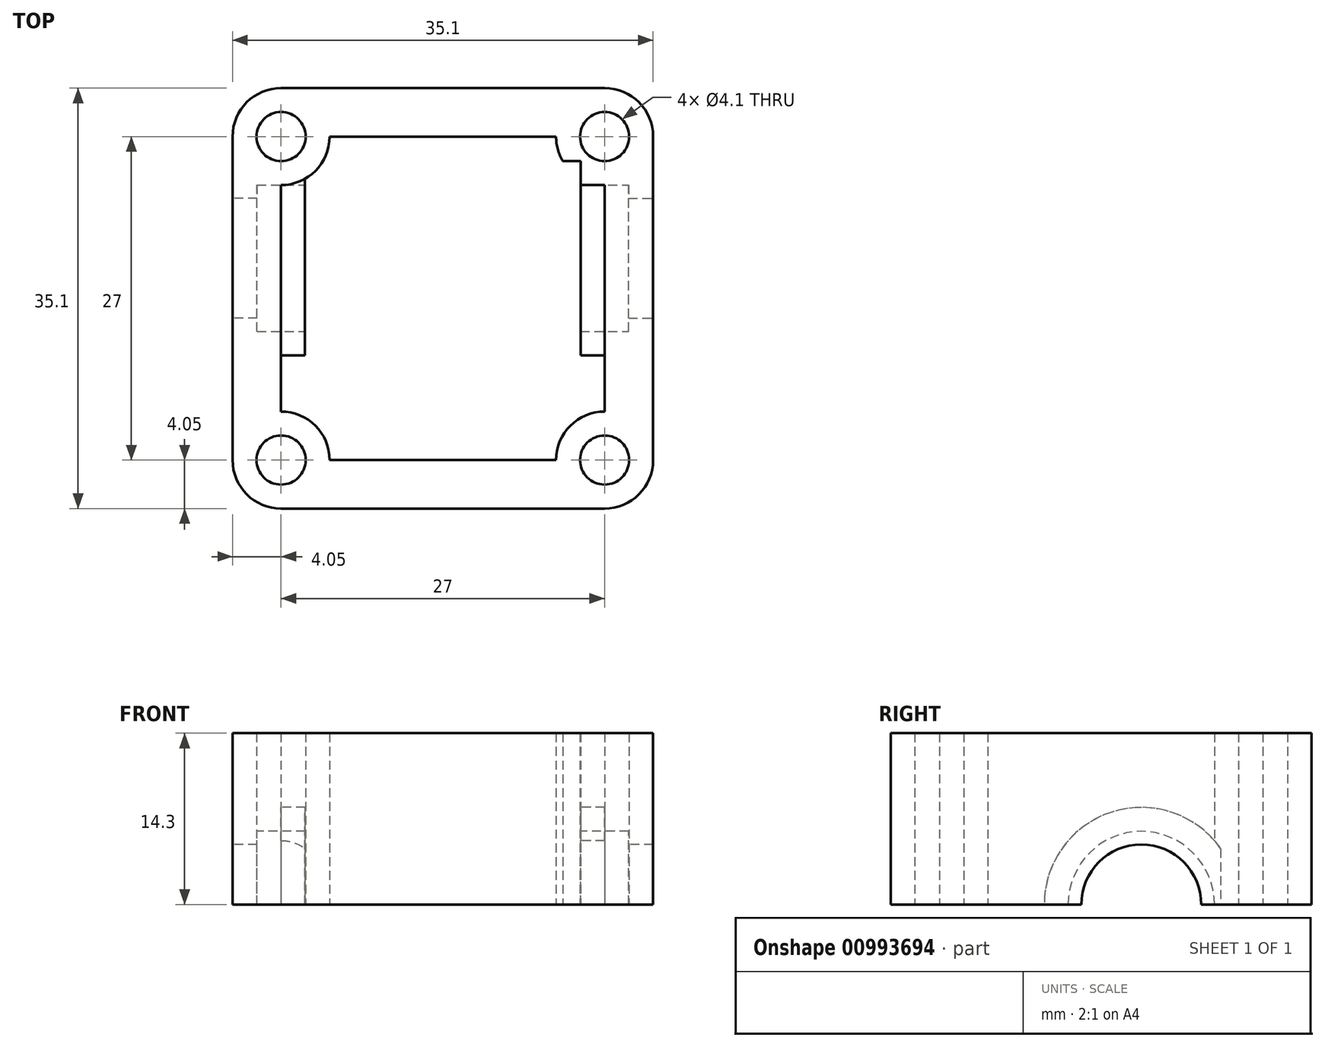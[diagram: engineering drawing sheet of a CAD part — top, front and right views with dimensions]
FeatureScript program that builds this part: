
annotation { "Feature Type Name" : "Feature", "Feature Type Description" : "" }
export const myFeature = defineFeature(function(context is Context, id is Id, definition is map)
    precondition{}
    {
        {
            var Q0;
            Q0=qCreatedBy(makeId("Top.planeOp"),FACE);
            var sketch = newSketch(context, id + "F0", { "sketchPlane" : qUnion([Q0])});
            skLineSegment(sketch, "E0.bottom", {"start": v(17.55, 17.55) * mm, "end": v(-17.55, 17.55) * mm});
            skLineSegment(sketch, "E0.top", {"start": v(17.55, -17.55) * mm, "end": v(-17.55, -17.55) * mm});
            skLineSegment(sketch, "E0.left", {"start": v(17.55, 17.55) * mm, "end": v(17.55, -17.55) * mm});
            skLineSegment(sketch, "E0.right", {"start": v(-17.55, 17.55) * mm, "end": v(-17.55, -17.55) * mm});
            skPoint(sketch, "E0.middle", {"position": v(0, 0) * mm});
            skLineSegment(sketch, "E1", {"start": v(0, 0) * mm, "end": v(0, 17.55) * mm, "construction": true});
            skLineSegment(sketch, "E2", {"start": v(0, 0) * mm, "end": v(-17.55, 0) * mm, "construction": true});
            skLineSegment(sketch, "E3.bottom", {"start": v(13.5, 13.5) * mm, "end": v(-13.5, 13.5) * mm});
            skLineSegment(sketch, "E3.top", {"start": v(13.5, -13.5) * mm, "end": v(-13.5, -13.5) * mm});
            skLineSegment(sketch, "E3.left", {"start": v(13.5, 13.5) * mm, "end": v(13.5, -13.5) * mm});
            skLineSegment(sketch, "E3.right", {"start": v(-13.5, 13.5) * mm, "end": v(-13.5, -13.5) * mm});
            skCircle(sketch, "E4", {"center": v(-13.5, 13.5) * mm, "radius": 2.05 * mm});
            skCircle(sketch, "E5", {"center": v(-13.5, 13.5) * mm, "radius": 4.05 * mm});
            skCircle(sketch, "E6.MirrorC", {"center": v(13.5, 13.5) * mm, "radius": 4.05 * mm});
            skCircle(sketch, "E7.MirrorC", {"center": v(13.5, 13.5) * mm, "radius": 2.05 * mm});
            skCircle(sketch, "E8.MirrorC", {"center": v(-13.5, -13.5) * mm, "radius": 4.05 * mm});
            skCircle(sketch, "E9.MirrorC", {"center": v(-13.5, -13.5) * mm, "radius": 2.05 * mm});
            skCircle(sketch, "E10.MirrorC", {"center": v(13.5, -13.5) * mm, "radius": 4.05 * mm});
            skCircle(sketch, "E11.MirrorC", {"center": v(13.5, -13.5) * mm, "radius": 2.05 * mm});
            skLineSegment(sketch, "E12", {"start": v(-15.5, 11.45) * mm, "end": v(15.5, 11.45) * mm});
            skLineSegment(sketch, "E13", {"start": v(15.5, 11.45) * mm, "end": v(15.5, -4.75) * mm});
            skLineSegment(sketch, "E14", {"start": v(15.5, -4.75) * mm, "end": v(-15.5, -4.75) * mm});
            skLineSegment(sketch, "E15", {"start": v(-15.5, 11.45) * mm, "end": v(-15.5, -4.75) * mm});
            skLineSegment(sketch, "E16", {"start": v(-15.5, 3.35) * mm, "end": v(15.5, 3.35) * mm});
            skLineSegment(sketch, "E17", {"start": v(15.5, -2.75) * mm, "end": v(-15.5, -2.75) * mm});
            skLineSegment(sketch, "E18", {"start": v(-15.5, 9.45) * mm, "end": v(15.5, 9.45) * mm});
            skLineSegment(sketch, "E19", {"start": v(-11.5, 11.45) * mm, "end": v(-11.5, -4.75) * mm});
            skLineSegment(sketch, "E20", {"start": v(11.5, 11.45) * mm, "end": v(11.5, -4.75) * mm});
            skLineSegment(sketch, "E21", {"start": v(-15.5, 3.35) * mm, "end": v(-17.55, 3.35) * mm});
            skLineSegment(sketch, "E22", {"start": v(15.5, 3.35) * mm, "end": v(17.55, 3.35) * mm});
            skLineSegment(sketch, "E23", {"start": v(-15.5, 8.35) * mm, "end": v(-17.55, 8.35) * mm});
            skLineSegment(sketch, "E24", {"start": v(15.5, 8.35) * mm, "end": v(17.55, 8.35) * mm});
            skSolve(sketch);
        }
        {
            var Q0;
            {var subQ0=sQuery(id+"F0.wireOp",EDGE,"E15");var subQ3=sQuery(id+"F0.wireOp",EDGE,"E18");var subQ5=makeQuery(id+"F0.imprint","INTERSECT",VERTEX,{"derivedFrom":[subQ0,subQ3]});Q0=makeQuery(id+"F0.imprint","IMPRINT",FACE,{"disambiguationData":[TD([[makeQuery(id+"F0.imprint","IMPRINT",EDGE,{"disambiguationData":[TD([[subQ5,1.0]])],"derivedFrom":subQ0}),1.0]])]});}
            var Q1;
            {var subQ0=sQuery(id+"F0.wireOp",EDGE,"E5");var subQ3=sQuery(id+"F0.wireOp",EDGE,"E3.bottom");var subQ4=makeQuery(id+"F0.imprint","INTERSECT",VERTEX,{"derivedFrom":[subQ3,subQ0]});Q1=makeQuery(id+"F0.imprint","IMPRINT",FACE,{"disambiguationData":[TD([[makeQuery(id+"F0.imprint","IMPRINT",EDGE,{"disambiguationData":[TD([[subQ4,-1.0]])],"derivedFrom":subQ3}),-1.0]])]});}
            var Q2;
            {var subQ0=sQuery(id+"F0.wireOp",EDGE,"E12");var subQ5=sQuery(id+"F0.wireOp",EDGE,"E15");var subQ7=makeQuery(id+"F0.imprint","INTERSECT",VERTEX,{"derivedFrom":[subQ0,subQ5]});Q2=makeQuery(id+"F0.imprint","IMPRINT",FACE,{"disambiguationData":[TD([[makeQuery(id+"F0.imprint","IMPRINT",EDGE,{"disambiguationData":[TD([[subQ7,-1.0]])],"derivedFrom":subQ5}),1.0]])]});}
            var Q3;
            {var subQ1=sQuery(id+"F0.wireOp",EDGE,"E0.right");var subQ7=sQuery(id+"F0.wireOp",EDGE,"E5");var subQ8=makeQuery(id+"F0.imprint","INTERSECT",VERTEX,{"derivedFrom":[subQ1,subQ7]});Q3=makeQuery(id+"F0.imprint","IMPRINT",FACE,{"disambiguationData":[TD([[makeQuery(id+"F0.imprint","IMPRINT",EDGE,{"disambiguationData":[TD([[subQ8,-1.0]])],"derivedFrom":subQ1}),1.0]])]});}
            var Q4;
            {var subQ0=sQuery(id+"F0.wireOp",EDGE,"E17");var subQ5=sQuery(id+"F0.wireOp",EDGE,"E15");var subQ7=makeQuery(id+"F0.imprint","INTERSECT",VERTEX,{"derivedFrom":[subQ5,subQ0]});Q4=makeQuery(id+"F0.imprint","IMPRINT",FACE,{"disambiguationData":[TD([[makeQuery(id+"F0.imprint","IMPRINT",EDGE,{"disambiguationData":[TD([[subQ7,1.0]])],"derivedFrom":subQ5}),1.0]])]});}
            var Q5;
            {var subQ0=sQuery(id+"F0.wireOp",EDGE,"E17");var subQ1=sQuery(id+"F0.wireOp",EDGE,"E3.right");var subQ2=makeQuery(id+"F0.imprint","INTERSECT",VERTEX,{"derivedFrom":[subQ1,subQ0]});Q5=makeQuery(id+"F0.imprint","IMPRINT",FACE,{"disambiguationData":[TD([[makeQuery(id+"F0.imprint","IMPRINT",EDGE,{"disambiguationData":[TD([[subQ2,-1.0]])],"derivedFrom":subQ1}),-1.0]])]});}
            var Q6;
            {var subQ0=sQuery(id+"F0.wireOp",EDGE,"E8.MirrorC");var subQ2=sQuery(id+"F0.wireOp",EDGE,"E3.top");var subQ3=makeQuery(id+"F0.imprint","INTERSECT",VERTEX,{"derivedFrom":[subQ2,subQ0]});Q6=makeQuery(id+"F0.imprint","IMPRINT",FACE,{"disambiguationData":[TD([[makeQuery(id+"F0.imprint","IMPRINT",EDGE,{"disambiguationData":[TD([[subQ3,-1.0]])],"derivedFrom":subQ2}),1.0]])]});}
            var Q7;
            {var subQ0=sQuery(id+"F0.wireOp",EDGE,"E10.MirrorC");var subQ1=sQuery(id+"F0.wireOp",EDGE,"E0.top");var subQ2=makeQuery(id+"F0.imprint","INTERSECT",VERTEX,{"derivedFrom":[subQ1,subQ0]});Q7=makeQuery(id+"F0.imprint","IMPRINT",FACE,{"disambiguationData":[TD([[makeQuery(id+"F0.imprint","IMPRINT",EDGE,{"disambiguationData":[TD([[subQ2,-1.0]])],"derivedFrom":subQ1}),-1.0]])]});}
            var Q8;
            {var subQ0=sQuery(id+"F0.wireOp",EDGE,"E8.MirrorC");var subQ1=sQuery(id+"F0.wireOp",EDGE,"E3.top");var subQ2=makeQuery(id+"F0.imprint","INTERSECT",VERTEX,{"derivedFrom":[subQ1,subQ0]});Q8=makeQuery(id+"F0.imprint","IMPRINT",FACE,{"disambiguationData":[TD([[makeQuery(id+"F0.imprint","IMPRINT",EDGE,{"disambiguationData":[TD([[subQ2,-1.0]])],"derivedFrom":subQ1}),-1.0]])]});}
            var Q9;
            {var subQ3=sQuery(id+"F0.wireOp",EDGE,"E3.top");var subQ7=sQuery(id+"F0.wireOp",EDGE,"E11.MirrorC");var subQ9=makeQuery(id+"F0.imprint","INTERSECT",VERTEX,{"derivedFrom":[subQ3,subQ7]});Q9=makeQuery(id+"F0.imprint","IMPRINT",FACE,{"disambiguationData":[TD([[makeQuery(id+"F0.imprint","IMPRINT",EDGE,{"disambiguationData":[TD([[subQ9,-1.0]])],"derivedFrom":subQ3}),1.0]])]});}
            var Q10;
            {var subQ0=sQuery(id+"F0.wireOp",EDGE,"E11.MirrorC");var subQ1=sQuery(id+"F0.wireOp",EDGE,"E3.top");var subQ2=makeQuery(id+"F0.imprint","INTERSECT",VERTEX,{"derivedFrom":[subQ1,subQ0]});Q10=makeQuery(id+"F0.imprint","IMPRINT",FACE,{"disambiguationData":[TD([[makeQuery(id+"F0.imprint","IMPRINT",EDGE,{"disambiguationData":[TD([[subQ2,-1.0]])],"derivedFrom":subQ1}),-1.0]])]});}
            var Q11;
            {var subQ5=sQuery(id+"F0.wireOp",EDGE,"E0.left");var subQ7=sQuery(id+"F0.wireOp",EDGE,"E6.MirrorC");var subQ8=makeQuery(id+"F0.imprint","INTERSECT",VERTEX,{"derivedFrom":[subQ5,subQ7]});Q11=makeQuery(id+"F0.imprint","IMPRINT",FACE,{"disambiguationData":[TD([[makeQuery(id+"F0.imprint","IMPRINT",EDGE,{"disambiguationData":[TD([[subQ8,-1.0]])],"derivedFrom":subQ5}),-1.0]])]});}
            var Q12;
            {var subQ0=sQuery(id+"F0.wireOp",EDGE,"E17");var subQ1=sQuery(id+"F0.wireOp",EDGE,"E3.left");var subQ2=makeQuery(id+"F0.imprint","INTERSECT",VERTEX,{"derivedFrom":[subQ1,subQ0]});Q12=makeQuery(id+"F0.imprint","IMPRINT",FACE,{"disambiguationData":[TD([[makeQuery(id+"F0.imprint","IMPRINT",EDGE,{"disambiguationData":[TD([[subQ2,-1.0]])],"derivedFrom":subQ1}),1.0]])]});}
            var Q13;
            {var subQ0=sQuery(id+"F0.wireOp",EDGE,"E17");var subQ5=sQuery(id+"F0.wireOp",EDGE,"E13");var subQ6=makeQuery(id+"F0.imprint","INTERSECT",VERTEX,{"derivedFrom":[subQ5,subQ0]});Q13=makeQuery(id+"F0.imprint","IMPRINT",FACE,{"disambiguationData":[TD([[makeQuery(id+"F0.imprint","IMPRINT",EDGE,{"disambiguationData":[TD([[subQ6,1.0]])],"derivedFrom":subQ5}),-1.0]])]});}
            var Q14;
            {var subQ0=sQuery(id+"F0.wireOp",EDGE,"E13");var subQ3=sQuery(id+"F0.wireOp",EDGE,"E18");var subQ5=makeQuery(id+"F0.imprint","INTERSECT",VERTEX,{"derivedFrom":[subQ0,subQ3]});Q14=makeQuery(id+"F0.imprint","IMPRINT",FACE,{"disambiguationData":[TD([[makeQuery(id+"F0.imprint","IMPRINT",EDGE,{"disambiguationData":[TD([[subQ5,1.0]])],"derivedFrom":subQ0}),-1.0]])]});}
            var Q15;
            {var subQ0=sQuery(id+"F0.wireOp",EDGE,"E12");var subQ5=sQuery(id+"F0.wireOp",EDGE,"E13");var subQ7=makeQuery(id+"F0.imprint","INTERSECT",VERTEX,{"derivedFrom":[subQ0,subQ5]});Q15=makeQuery(id+"F0.imprint","IMPRINT",FACE,{"disambiguationData":[TD([[makeQuery(id+"F0.imprint","IMPRINT",EDGE,{"disambiguationData":[TD([[subQ7,-1.0]])],"derivedFrom":subQ5}),-1.0]])]});}
            var Q16;
            {var subQ0=sQuery(id+"F0.wireOp",EDGE,"E12");var subQ5=sQuery(id+"F0.wireOp",EDGE,"E20");var subQ7=makeQuery(id+"F0.imprint","INTERSECT",VERTEX,{"derivedFrom":[subQ0,subQ5]});Q16=makeQuery(id+"F0.imprint","IMPRINT",FACE,{"disambiguationData":[TD([[makeQuery(id+"F0.imprint","IMPRINT",EDGE,{"disambiguationData":[TD([[subQ7,-1.0]])],"derivedFrom":subQ5}),1.0]])]});}
            var Q17;
            {var subQ0=sQuery(id+"F0.wireOp",EDGE,"E20");var subQ1=sQuery(id+"F0.wireOp",EDGE,"E6.MirrorC");var subQ2=makeQuery(id+"F0.imprint","INTERSECT",VERTEX,{"derivedFrom":[subQ1,subQ0]});Q17=makeQuery(id+"F0.imprint","IMPRINT",FACE,{"disambiguationData":[TD([[makeQuery(id+"F0.imprint","IMPRINT",EDGE,{"disambiguationData":[TD([[subQ2,-1.0]])],"derivedFrom":subQ1}),-1.0]])]});}
            var Q18;
            {var subQ4=sQuery(id+"F0.wireOp",EDGE,"E3.bottom");var subQ6=sQuery(id+"F0.wireOp",EDGE,"E7.MirrorC");var subQ7=makeQuery(id+"F0.imprint","INTERSECT",VERTEX,{"derivedFrom":[subQ4,subQ6]});Q18=makeQuery(id+"F0.imprint","IMPRINT",FACE,{"disambiguationData":[TD([[makeQuery(id+"F0.imprint","IMPRINT",EDGE,{"disambiguationData":[TD([[subQ7,-1.0]])],"derivedFrom":subQ4}),1.0]])]});}
            var Q19;
            {var subQ5=sQuery(id+"F0.wireOp",EDGE,"E7.MirrorC");var subQ6=sQuery(id+"F0.wireOp",EDGE,"E3.bottom");var subQ7=makeQuery(id+"F0.imprint","INTERSECT",VERTEX,{"derivedFrom":[subQ6,subQ5]});Q19=makeQuery(id+"F0.imprint","IMPRINT",FACE,{"disambiguationData":[TD([[makeQuery(id+"F0.imprint","IMPRINT",EDGE,{"disambiguationData":[TD([[subQ7,-1.0]])],"derivedFrom":subQ6}),-1.0]])]});}
            var Q20;
            {var subQ0=sQuery(id+"F0.wireOp",EDGE,"E6.MirrorC");var subQ1=sQuery(id+"F0.wireOp",EDGE,"E0.bottom");var subQ2=makeQuery(id+"F0.imprint","INTERSECT",VERTEX,{"derivedFrom":[subQ1,subQ0]});Q20=makeQuery(id+"F0.imprint","IMPRINT",FACE,{"disambiguationData":[TD([[makeQuery(id+"F0.imprint","IMPRINT",EDGE,{"disambiguationData":[TD([[subQ2,-1.0]])],"derivedFrom":subQ1}),1.0]])]});}
            var Q21;
            {var subQ0=sQuery(id+"F0.wireOp",EDGE,"E5");var subQ1=sQuery(id+"F0.wireOp",EDGE,"E3.bottom");var subQ2=makeQuery(id+"F0.imprint","INTERSECT",VERTEX,{"derivedFrom":[subQ1,subQ0]});Q21=makeQuery(id+"F0.imprint","IMPRINT",FACE,{"disambiguationData":[TD([[makeQuery(id+"F0.imprint","IMPRINT",EDGE,{"disambiguationData":[TD([[subQ2,-1.0]])],"derivedFrom":subQ1}),1.0]])]});}
            var Q22;
            {var subQ0=sQuery(id+"F0.wireOp",EDGE,"E12");var subQ5=sQuery(id+"F0.wireOp",EDGE,"E19");var subQ7=makeQuery(id+"F0.imprint","INTERSECT",VERTEX,{"derivedFrom":[subQ0,subQ5]});Q22=makeQuery(id+"F0.imprint","IMPRINT",FACE,{"disambiguationData":[TD([[makeQuery(id+"F0.imprint","IMPRINT",EDGE,{"disambiguationData":[TD([[subQ7,-1.0]])],"derivedFrom":subQ5}),-1.0]])]});}
            var Q23;
            {var subQ0=sQuery(id+"F0.wireOp",EDGE,"E19");var subQ1=sQuery(id+"F0.wireOp",EDGE,"E5");var subQ2=makeQuery(id+"F0.imprint","INTERSECT",VERTEX,{"derivedFrom":[subQ1,subQ0]});Q23=makeQuery(id+"F0.imprint","IMPRINT",FACE,{"disambiguationData":[TD([[makeQuery(id+"F0.imprint","IMPRINT",EDGE,{"disambiguationData":[TD([[subQ2,-1.0]])],"derivedFrom":subQ1}),1.0]])]});}
            var Q24;
            {var subQ10=sQuery(id+"F0.wireOp",EDGE,"E21");Q24=makeQuery(id+"F0.imprint","IMPRINT",FACE,{"disambiguationData":[TD([[makeQuery(id+"F0.imprint","IMPRINT",EDGE,{"derivedFrom":subQ10}),1.0]])]});}
            var Q25;
            {var subQ0=sQuery(id+"F0.wireOp",EDGE,"E21");Q25=makeQuery(id+"F0.imprint","IMPRINT",FACE,{"disambiguationData":[TD([[makeQuery(id+"F0.imprint","IMPRINT",EDGE,{"derivedFrom":subQ0}),-1.0]])]});}
            var Q26;
            {var subQ1=sQuery(id+"F0.wireOp",EDGE,"E15");var subQ4=sQuery(id+"F0.wireOp",EDGE,"E18");var subQ5=makeQuery(id+"F0.imprint","INTERSECT",VERTEX,{"derivedFrom":[subQ1,subQ4]});Q26=makeQuery(id+"F0.imprint","IMPRINT",FACE,{"disambiguationData":[TD([[makeQuery(id+"F0.imprint","IMPRINT",EDGE,{"disambiguationData":[TD([[subQ5,-1.0]])],"derivedFrom":subQ1}),1.0]])]});}
            var Q27;
            {var subQ0=sQuery(id+"F0.wireOp",EDGE,"E22");Q27=makeQuery(id+"F0.imprint","IMPRINT",FACE,{"disambiguationData":[TD([[makeQuery(id+"F0.imprint","IMPRINT",EDGE,{"derivedFrom":subQ0}),1.0]])]});}
            var Q28;
            {var subQ1=sQuery(id+"F0.wireOp",EDGE,"E13");var subQ6=sQuery(id+"F0.wireOp",EDGE,"E18");var subQ7=makeQuery(id+"F0.imprint","INTERSECT",VERTEX,{"derivedFrom":[subQ1,subQ6]});Q28=makeQuery(id+"F0.imprint","IMPRINT",FACE,{"disambiguationData":[TD([[makeQuery(id+"F0.imprint","IMPRINT",EDGE,{"disambiguationData":[TD([[subQ7,-1.0]])],"derivedFrom":subQ1}),-1.0]])]});}
            var Q29;
            {var subQ0=sQuery(id+"F0.wireOp",EDGE,"E22");Q29=makeQuery(id+"F0.imprint","IMPRINT",FACE,{"disambiguationData":[TD([[makeQuery(id+"F0.imprint","IMPRINT",EDGE,{"derivedFrom":subQ0}),-1.0]])]});}
            var Q30;
            {var subQ0=sQuery(id+"F0.wireOp",EDGE,"E18");var subQ1=sQuery(id+"F0.wireOp",EDGE,"E5");var subQ2=makeQuery(id+"F0.imprint","INTERSECT",VERTEX,{"derivedFrom":[subQ1,subQ0]});Q30=makeQuery(id+"F0.imprint","IMPRINT",FACE,{"disambiguationData":[TD([[makeQuery(id+"F0.imprint","IMPRINT",EDGE,{"disambiguationData":[TD([[subQ2,-1.0]])],"derivedFrom":subQ1}),1.0]])]});}
            var Q31;
            {var subQ4=sQuery(id+"F0.wireOp",EDGE,"E5");var subQ6=sQuery(id+"F0.wireOp",EDGE,"E3.right");var subQ7=makeQuery(id+"F0.imprint","INTERSECT",VERTEX,{"derivedFrom":[subQ6,subQ4]});Q31=makeQuery(id+"F0.imprint","IMPRINT",FACE,{"disambiguationData":[TD([[makeQuery(id+"F0.imprint","IMPRINT",EDGE,{"disambiguationData":[TD([[subQ7,-1.0]])],"derivedFrom":subQ6}),-1.0]])]});}
            var Q32;
            {var subQ4=sQuery(id+"F0.wireOp",EDGE,"E6.MirrorC");var subQ6=sQuery(id+"F0.wireOp",EDGE,"E3.left");var subQ7=makeQuery(id+"F0.imprint","INTERSECT",VERTEX,{"derivedFrom":[subQ6,subQ4]});Q32=makeQuery(id+"F0.imprint","IMPRINT",FACE,{"disambiguationData":[TD([[makeQuery(id+"F0.imprint","IMPRINT",EDGE,{"disambiguationData":[TD([[subQ7,-1.0]])],"derivedFrom":subQ6}),1.0]])]});}
            var Q33;
            {var subQ0=sQuery(id+"F0.wireOp",EDGE,"E18");var subQ1=sQuery(id+"F0.wireOp",EDGE,"E6.MirrorC");var subQ2=makeQuery(id+"F0.imprint","INTERSECT",VERTEX,{"derivedFrom":[subQ1,subQ0]});Q33=makeQuery(id+"F0.imprint","IMPRINT",FACE,{"disambiguationData":[TD([[makeQuery(id+"F0.imprint","IMPRINT",EDGE,{"disambiguationData":[TD([[subQ2,-1.0]])],"derivedFrom":subQ1}),-1.0]])]});}
            extrude(context, id + "F1", {"entities" : qUnion([Q0, Q1, Q2, Q3, Q4, Q5, Q6, Q7, Q8, Q9, Q10, Q11, Q12, Q13, Q14, Q15, Q16, Q17, Q18, Q19, Q20, Q21, Q22, Q23, Q24, Q25, Q26, Q27, Q28, Q29, Q30, Q31, Q32, Q33]), "depth" : ((28 / 2) + 0.3) * mm, "offsetDistance" : 25 * mm});
        }
        {
            var Q0;
            {var subQ0=sQuery(id+"F0.wireOp",EDGE,"E21");Q0=makeQuery(id+"F0.imprint","IMPRINT",FACE,{"disambiguationData":[TD([[makeQuery(id+"F0.imprint","IMPRINT",EDGE,{"derivedFrom":subQ0}),-1.0]])]});}
            var Q1;
            {var subQ1=sQuery(id+"F0.wireOp",EDGE,"E15");var subQ4=sQuery(id+"F0.wireOp",EDGE,"E18");var subQ5=makeQuery(id+"F0.imprint","INTERSECT",VERTEX,{"derivedFrom":[subQ1,subQ4]});Q1=makeQuery(id+"F0.imprint","IMPRINT",FACE,{"disambiguationData":[TD([[makeQuery(id+"F0.imprint","IMPRINT",EDGE,{"disambiguationData":[TD([[subQ5,-1.0]])],"derivedFrom":subQ1}),1.0]])]});}
            var Q2;
            {var subQ0=sQuery(id+"F0.wireOp",EDGE,"E16");var subQ1=sQuery(id+"F0.wireOp",EDGE,"E3.right");var subQ2=makeQuery(id+"F0.imprint","INTERSECT",VERTEX,{"derivedFrom":[subQ1,subQ0]});Q2=makeQuery(id+"F0.imprint","IMPRINT",FACE,{"disambiguationData":[TD([[makeQuery(id+"F0.imprint","IMPRINT",EDGE,{"disambiguationData":[TD([[subQ2,-1.0]])],"derivedFrom":subQ0}),1.0]])]});}
            var Q3;
            {var subQ0=sQuery(id+"F0.wireOp",EDGE,"E12");var subQ5=sQuery(id+"F0.wireOp",EDGE,"E19");var subQ7=makeQuery(id+"F0.imprint","INTERSECT",VERTEX,{"derivedFrom":[subQ0,subQ5]});Q3=makeQuery(id+"F0.imprint","IMPRINT",FACE,{"disambiguationData":[TD([[makeQuery(id+"F0.imprint","IMPRINT",EDGE,{"disambiguationData":[TD([[subQ7,-1.0]])],"derivedFrom":subQ5}),-1.0]])]});}
            var Q4;
            {var subQ0=sQuery(id+"F0.wireOp",EDGE,"E12");var subQ5=sQuery(id+"F0.wireOp",EDGE,"E15");var subQ6=makeQuery(id+"F0.imprint","INTERSECT",VERTEX,{"derivedFrom":[subQ0,subQ5]});Q4=makeQuery(id+"F0.imprint","IMPRINT",FACE,{"disambiguationData":[TD([[makeQuery(id+"F0.imprint","IMPRINT",EDGE,{"disambiguationData":[TD([[subQ6,-1.0]])],"derivedFrom":subQ5}),1.0]])]});}
            var Q5;
            {var subQ0=sQuery(id+"F0.wireOp",EDGE,"E12");var subQ5=sQuery(id+"F0.wireOp",EDGE,"E20");var subQ6=makeQuery(id+"F0.imprint","INTERSECT",VERTEX,{"derivedFrom":[subQ0,subQ5]});Q5=makeQuery(id+"F0.imprint","IMPRINT",FACE,{"disambiguationData":[TD([[makeQuery(id+"F0.imprint","IMPRINT",EDGE,{"disambiguationData":[TD([[subQ6,-1.0]])],"derivedFrom":subQ5}),1.0]])]});}
            var Q6;
            {var subQ0=sQuery(id+"F0.wireOp",EDGE,"E16");var subQ1=sQuery(id+"F0.wireOp",EDGE,"E3.left");var subQ2=makeQuery(id+"F0.imprint","INTERSECT",VERTEX,{"derivedFrom":[subQ1,subQ0]});Q6=makeQuery(id+"F0.imprint","IMPRINT",FACE,{"disambiguationData":[TD([[makeQuery(id+"F0.imprint","IMPRINT",EDGE,{"disambiguationData":[TD([[subQ2,1.0]])],"derivedFrom":subQ0}),1.0]])]});}
            var Q7;
            {var subQ1=sQuery(id+"F0.wireOp",EDGE,"E13");var subQ6=sQuery(id+"F0.wireOp",EDGE,"E18");var subQ7=makeQuery(id+"F0.imprint","INTERSECT",VERTEX,{"derivedFrom":[subQ1,subQ6]});Q7=makeQuery(id+"F0.imprint","IMPRINT",FACE,{"disambiguationData":[TD([[makeQuery(id+"F0.imprint","IMPRINT",EDGE,{"disambiguationData":[TD([[subQ7,-1.0]])],"derivedFrom":subQ1}),-1.0]])]});}
            var Q8;
            {var subQ0=sQuery(id+"F0.wireOp",EDGE,"E12");var subQ5=sQuery(id+"F0.wireOp",EDGE,"E13");var subQ7=makeQuery(id+"F0.imprint","INTERSECT",VERTEX,{"derivedFrom":[subQ0,subQ5]});Q8=makeQuery(id+"F0.imprint","IMPRINT",FACE,{"disambiguationData":[TD([[makeQuery(id+"F0.imprint","IMPRINT",EDGE,{"disambiguationData":[TD([[subQ7,-1.0]])],"derivedFrom":subQ5}),-1.0]])]});}
            var Q9;
            {var subQ0=sQuery(id+"F0.wireOp",EDGE,"E22");Q9=makeQuery(id+"F0.imprint","IMPRINT",FACE,{"disambiguationData":[TD([[makeQuery(id+"F0.imprint","IMPRINT",EDGE,{"derivedFrom":subQ0}),1.0]])]});}
            var Q10;
            {var subQ0=sQuery(id+"F0.wireOp",EDGE,"E19");var subQ1=sQuery(id+"F0.wireOp",EDGE,"E5");var subQ2=makeQuery(id+"F0.imprint","INTERSECT",VERTEX,{"derivedFrom":[subQ1,subQ0]});Q10=makeQuery(id+"F0.imprint","IMPRINT",FACE,{"disambiguationData":[TD([[makeQuery(id+"F0.imprint","IMPRINT",EDGE,{"disambiguationData":[TD([[subQ2,-1.0]])],"derivedFrom":subQ0}),-1.0]])]});}
            var Q11;
            {var subQ0=sQuery(id+"F0.wireOp",EDGE,"E15");var subQ3=sQuery(id+"F0.wireOp",EDGE,"E18");var subQ5=makeQuery(id+"F0.imprint","INTERSECT",VERTEX,{"derivedFrom":[subQ0,subQ3]});Q11=makeQuery(id+"F0.imprint","IMPRINT",FACE,{"disambiguationData":[TD([[makeQuery(id+"F0.imprint","IMPRINT",EDGE,{"disambiguationData":[TD([[subQ5,1.0]])],"derivedFrom":subQ0}),1.0]])]});}
            var Q12;
            {var subQ0=sQuery(id+"F0.wireOp",EDGE,"E13");var subQ3=sQuery(id+"F0.wireOp",EDGE,"E18");var subQ5=makeQuery(id+"F0.imprint","INTERSECT",VERTEX,{"derivedFrom":[subQ0,subQ3]});Q12=makeQuery(id+"F0.imprint","IMPRINT",FACE,{"disambiguationData":[TD([[makeQuery(id+"F0.imprint","IMPRINT",EDGE,{"disambiguationData":[TD([[subQ5,1.0]])],"derivedFrom":subQ0}),-1.0]])]});}
            var Q13;
            {var subQ0=sQuery(id+"F0.wireOp",EDGE,"E20");var subQ1=sQuery(id+"F0.wireOp",EDGE,"E6.MirrorC");var subQ2=makeQuery(id+"F0.imprint","INTERSECT",VERTEX,{"derivedFrom":[subQ1,subQ0]});Q13=makeQuery(id+"F0.imprint","IMPRINT",FACE,{"disambiguationData":[TD([[makeQuery(id+"F0.imprint","IMPRINT",EDGE,{"disambiguationData":[TD([[subQ2,-1.0]])],"derivedFrom":subQ0}),1.0]])]});}
            var Q14;
            {var subQ4=sQuery(id+"F0.wireOp",EDGE,"E5");var subQ6=sQuery(id+"F0.wireOp",EDGE,"E3.right");var subQ7=makeQuery(id+"F0.imprint","INTERSECT",VERTEX,{"derivedFrom":[subQ6,subQ4]});Q14=makeQuery(id+"F0.imprint","IMPRINT",FACE,{"disambiguationData":[TD([[makeQuery(id+"F0.imprint","IMPRINT",EDGE,{"disambiguationData":[TD([[subQ7,-1.0]])],"derivedFrom":subQ6}),-1.0]])]});}
            var Q15;
            {var subQ0=sQuery(id+"F0.wireOp",EDGE,"E18");var subQ1=sQuery(id+"F0.wireOp",EDGE,"E3.right");var subQ2=makeQuery(id+"F0.imprint","INTERSECT",VERTEX,{"derivedFrom":[subQ1,subQ0]});Q15=makeQuery(id+"F0.imprint","IMPRINT",FACE,{"disambiguationData":[TD([[makeQuery(id+"F0.imprint","IMPRINT",EDGE,{"disambiguationData":[TD([[subQ2,-1.0]])],"derivedFrom":subQ1}),1.0]])]});}
            var Q16;
            {var subQ4=sQuery(id+"F0.wireOp",EDGE,"E6.MirrorC");var subQ6=sQuery(id+"F0.wireOp",EDGE,"E3.left");var subQ7=makeQuery(id+"F0.imprint","INTERSECT",VERTEX,{"derivedFrom":[subQ6,subQ4]});Q16=makeQuery(id+"F0.imprint","IMPRINT",FACE,{"disambiguationData":[TD([[makeQuery(id+"F0.imprint","IMPRINT",EDGE,{"disambiguationData":[TD([[subQ7,-1.0]])],"derivedFrom":subQ6}),1.0]])]});}
            var Q17;
            {var subQ0=sQuery(id+"F0.wireOp",EDGE,"E18");var subQ1=sQuery(id+"F0.wireOp",EDGE,"E3.left");var subQ2=makeQuery(id+"F0.imprint","INTERSECT",VERTEX,{"derivedFrom":[subQ1,subQ0]});Q17=makeQuery(id+"F0.imprint","IMPRINT",FACE,{"disambiguationData":[TD([[makeQuery(id+"F0.imprint","IMPRINT",EDGE,{"disambiguationData":[TD([[subQ2,-1.0]])],"derivedFrom":subQ1}),-1.0]])]});}
            var Q18;
            Q18=sQuery(id+"F0.wireOp",EDGE,"E16");
            revolve(context, id + "F2", {"operationType" : NewBodyOperationType.ADD, "surfaceOperationType" : NewSurfaceOperationType.NEW, "entities" : qUnion([Q0, Q1, Q2, Q3, Q4, Q5, Q6, Q7, Q8, Q9, Q10, Q11, Q12, Q13, Q14, Q15, Q16, Q17]), "axis" : qUnion([Q18]), "revolveType" : RevolveType.ONE_DIRECTION, "angle" : 180 * degree});
        }
        {
            var Q0;
            {var subQ1=sQuery(id+"F0.wireOp",EDGE,"E13");var subQ6=sQuery(id+"F0.wireOp",EDGE,"E18");var subQ7=makeQuery(id+"F0.imprint","INTERSECT",VERTEX,{"derivedFrom":[subQ1,subQ6]});Q0=makeQuery(id+"F0.imprint","IMPRINT",FACE,{"disambiguationData":[TD([[makeQuery(id+"F0.imprint","IMPRINT",EDGE,{"disambiguationData":[TD([[subQ7,-1.0]])],"derivedFrom":subQ1}),-1.0]])]});}
            var Q1;
            {var subQ0=sQuery(id+"F0.wireOp",EDGE,"E22");Q1=makeQuery(id+"F0.imprint","IMPRINT",FACE,{"disambiguationData":[TD([[makeQuery(id+"F0.imprint","IMPRINT",EDGE,{"derivedFrom":subQ0}),1.0]])]});}
            var Q2;
            {var subQ0=sQuery(id+"F0.wireOp",EDGE,"E16");var subQ1=sQuery(id+"F0.wireOp",EDGE,"E3.left");var subQ2=makeQuery(id+"F0.imprint","INTERSECT",VERTEX,{"derivedFrom":[subQ1,subQ0]});Q2=makeQuery(id+"F0.imprint","IMPRINT",FACE,{"disambiguationData":[TD([[makeQuery(id+"F0.imprint","IMPRINT",EDGE,{"disambiguationData":[TD([[subQ2,1.0]])],"derivedFrom":subQ0}),1.0]])]});}
            var Q3;
            {var subQ0=sQuery(id+"F0.wireOp",EDGE,"E16");var subQ1=sQuery(id+"F0.wireOp",EDGE,"E3.right");var subQ2=makeQuery(id+"F0.imprint","INTERSECT",VERTEX,{"derivedFrom":[subQ1,subQ0]});Q3=makeQuery(id+"F0.imprint","IMPRINT",FACE,{"disambiguationData":[TD([[makeQuery(id+"F0.imprint","IMPRINT",EDGE,{"disambiguationData":[TD([[subQ2,-1.0]])],"derivedFrom":subQ0}),1.0]])]});}
            var Q4;
            {var subQ1=sQuery(id+"F0.wireOp",EDGE,"E15");var subQ4=sQuery(id+"F0.wireOp",EDGE,"E18");var subQ5=makeQuery(id+"F0.imprint","INTERSECT",VERTEX,{"derivedFrom":[subQ1,subQ4]});Q4=makeQuery(id+"F0.imprint","IMPRINT",FACE,{"disambiguationData":[TD([[makeQuery(id+"F0.imprint","IMPRINT",EDGE,{"disambiguationData":[TD([[subQ5,-1.0]])],"derivedFrom":subQ1}),1.0]])]});}
            var Q5;
            {var subQ0=sQuery(id+"F0.wireOp",EDGE,"E21");Q5=makeQuery(id+"F0.imprint","IMPRINT",FACE,{"disambiguationData":[TD([[makeQuery(id+"F0.imprint","IMPRINT",EDGE,{"derivedFrom":subQ0}),-1.0]])]});}
            var Q6;
            {var subQ4=sQuery(id+"F0.wireOp",EDGE,"E5");var subQ6=sQuery(id+"F0.wireOp",EDGE,"E3.right");var subQ7=makeQuery(id+"F0.imprint","INTERSECT",VERTEX,{"derivedFrom":[subQ6,subQ4]});Q6=makeQuery(id+"F0.imprint","IMPRINT",FACE,{"disambiguationData":[TD([[makeQuery(id+"F0.imprint","IMPRINT",EDGE,{"disambiguationData":[TD([[subQ7,-1.0]])],"derivedFrom":subQ6}),-1.0]])]});}
            var Q7;
            {var subQ4=sQuery(id+"F0.wireOp",EDGE,"E6.MirrorC");var subQ6=sQuery(id+"F0.wireOp",EDGE,"E3.left");var subQ7=makeQuery(id+"F0.imprint","INTERSECT",VERTEX,{"derivedFrom":[subQ6,subQ4]});Q7=makeQuery(id+"F0.imprint","IMPRINT",FACE,{"disambiguationData":[TD([[makeQuery(id+"F0.imprint","IMPRINT",EDGE,{"disambiguationData":[TD([[subQ7,-1.0]])],"derivedFrom":subQ6}),1.0]])]});}
            var Q8;
            {var subQ0=sQuery(id+"F0.wireOp",EDGE,"E18");var subQ1=sQuery(id+"F0.wireOp",EDGE,"E3.left");var subQ2=makeQuery(id+"F0.imprint","INTERSECT",VERTEX,{"derivedFrom":[subQ1,subQ0]});Q8=makeQuery(id+"F0.imprint","IMPRINT",FACE,{"disambiguationData":[TD([[makeQuery(id+"F0.imprint","IMPRINT",EDGE,{"disambiguationData":[TD([[subQ2,-1.0]])],"derivedFrom":subQ1}),-1.0]])]});}
            var Q9;
            {var subQ0=sQuery(id+"F0.wireOp",EDGE,"E18");var subQ1=sQuery(id+"F0.wireOp",EDGE,"E3.right");var subQ2=makeQuery(id+"F0.imprint","INTERSECT",VERTEX,{"derivedFrom":[subQ1,subQ0]});Q9=makeQuery(id+"F0.imprint","IMPRINT",FACE,{"disambiguationData":[TD([[makeQuery(id+"F0.imprint","IMPRINT",EDGE,{"disambiguationData":[TD([[subQ2,-1.0]])],"derivedFrom":subQ1}),1.0]])]});}
            var Q10;
            Q10=sQuery(id+"F0.wireOp",EDGE,"E16");
            revolve(context, id + "F3", {"operationType" : NewBodyOperationType.REMOVE, "surfaceOperationType" : NewSurfaceOperationType.NEW, "entities" : qUnion([Q0, Q1, Q2, Q3, Q4, Q5, Q6, Q7, Q8, Q9]), "axis" : qUnion([Q10]), "revolveType" : RevolveType.ONE_DIRECTION, "angle" : 180 * degree});
        }
    });
